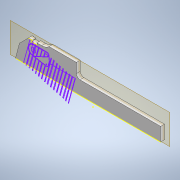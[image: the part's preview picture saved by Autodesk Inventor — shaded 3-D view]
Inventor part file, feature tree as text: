
AUTODESK INVENTOR PART (.ipt)
format: ipt  version: 2022 (Build 260153000, 153)  size: 396,288 bytes
history: native  units: in
note: dims shown in document units (in); Inventor stores cm internally (conversion verified against a paired STEP export)
features: extrude x4, sketch x2, sheet_metal_op x1, plane x1, mirror x1, other x1
ambient origin geometry x8: Origin, YZ Plane, XZ Plane, XY Plane, X Axis, Y Axis, Z Axis, Center Point
bodies: Solid1 (feature_tree)
feature tree (10):
  sheet_metal_op  "Face1"
  sketch  "Sketch2"  dims[d7=0.0039in d8=0.0in d9=0.0039in d10=0.0in d11=0.0039in d12=0.0in]
  extrude  "Extrusion1"  Depth=0.0039in TaperAngle=0.0deg
  extrude  "Extrusion4"  Depth=0.0039in TaperAngle=0.0deg
  extrude  "Extrusion5"  Depth=0.0039in TaperAngle=0.0deg
  extrude  "Extrusion6"  [1 undecoded]
  plane  "Work Plane1"
  mirror  "Mirror1"
  sketch  "Sketch1"  dims[d0=0.0591in d1=0.0039in d2=0.0in]
  other  "Plate1"
note: 1 required parameter value undecoded (feature->parameter linkage not recoverable at this tier; creation-order binding heuristic only, values carry confidence <= 0.55)
